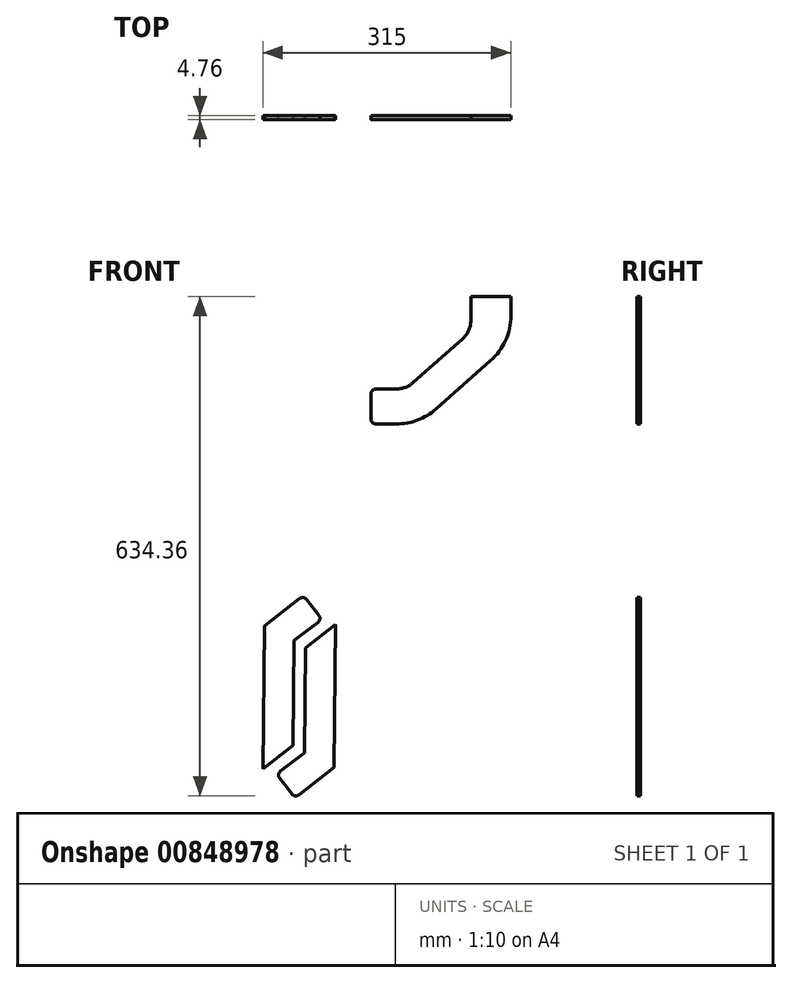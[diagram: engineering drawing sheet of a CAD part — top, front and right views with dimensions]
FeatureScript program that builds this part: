
annotation { "Feature Type Name" : "Feature", "Feature Type Description" : "" }
export const myFeature = defineFeature(function(context is Context, id is Id, definition is map)
    precondition{}
    {
        {
            var Q0;
            Q0=qCreatedBy(makeId("Front.planeOp"),FACE);
            var sketch = newSketch(context, id + "F0", { "sketchPlane" : qUnion([Q0])});
            skLineSegment(sketch, "E0.bottom", {"start": v(6.35, 0) * mm, "end": v(32.42, 0) * mm});
            skLineSegment(sketch, "E0.top", {"start": v(127, 161.93) * mm, "end": v(177.8, 161.93) * mm});
            skLineSegment(sketch, "E0.left", {"start": v(0, 6.35) * mm, "end": v(0, 38.1) * mm});
            skLineSegment(sketch, "E0.right", {"start": v(177.8, 137.4) * mm, "end": v(177.8, 161.93) * mm});
            skLineSegment(sketch, "E1", {"start": v(6.35, 44.45) * mm, "end": v(32.42, 44.45) * mm});
            skLineSegment(sketch, "E2", {"start": v(53.46, 52.42) * mm, "end": v(116.29, 108) * mm});
            skLineSegment(sketch, "E3", {"start": v(127, 131.78) * mm, "end": v(127, 161.93) * mm});
            skLineSegment(sketch, "E4.0", {"start": v(82.91, 19.13) * mm, "end": v(152.09, 80.32) * mm});
            skArc(sketch, "E5.filletArc", {"start": v(32.42, 0) * mm, "mid": v(59.42, 4.94) * mm, "end": v(82.91, 19.13) * mm});
            skArc(sketch, "E6.filletArc", {"start": v(152.09, 80.32) * mm, "mid": v(171.08, 106.1) * mm, "end": v(177.8, 137.4) * mm});
            skPoint(sketch, "E7.visualSharp", {"position": v(44.45, 44.45) * mm});
            skArc(sketch, "E7.filletArc", {"start": v(32.42, 44.45) * mm, "mid": v(43.67, 46.5) * mm, "end": v(53.46, 52.42) * mm});
            skPoint(sketch, "E8.visualSharp", {"position": v(127, 117.48) * mm});
            skArc(sketch, "E8.filletArc", {"start": v(116.29, 108) * mm, "mid": v(124.2, 118.74) * mm, "end": v(127, 131.78) * mm});
            skPoint(sketch, "E9.visualSharp", {"position": v(0, 44.45) * mm});
            skArc(sketch, "E9.filletArc", {"start": v(6.35, 44.45) * mm, "mid": v(1.86, 42.6) * mm, "end": v(0, 38.1) * mm});
            skPoint(sketch, "E10.visualSharp", {"position": v(0, 0) * mm});
            skArc(sketch, "E10.filletArc", {"start": v(0, 6.35) * mm, "mid": v(1.86, 1.86) * mm, "end": v(6.35, 0) * mm});
            skArc(sketch, "E11.MirrorCS", {"start": v(-114.78, -440.95) * mm, "mid": v(-117.2, -445.17) * mm, "end": v(-115.92, -449.86) * mm});
            skArc(sketch, "E12.MirrorCS", {"start": v(-100.4, -469.96) * mm, "mid": v(-96.18, -472.38) * mm, "end": v(-91.5, -471.11) * mm});
            skPoint(sketch, "E13.MirrorP", {"position": v(-84.62, -417.67) * mm});
            skLineSegment(sketch, "E14.MirrorCS", {"start": v(-83.27, -284.33) * mm, "end": v(-44.86, -254.68) * mm});
            skLineSegment(sketch, "E15.MirrorCS", {"start": v(-83.27, -284.33) * mm, "end": v(-84.62, -417.67) * mm});
            skLineSegment(sketch, "E16.MirrorCS", {"start": v(-114.78, -440.95) * mm, "end": v(-84.62, -417.67) * mm});
            skLineSegment(sketch, "E17.MirrorCS", {"start": v(-91.5, -471.11) * mm, "end": v(-46.7, -436.54) * mm});
            skLineSegment(sketch, "E18.MirrorCS", {"start": v(-100.4, -469.96) * mm, "end": v(-115.92, -449.86) * mm});
            skLineSegment(sketch, "E19.0", {"start": v(-44.86, -254.68) * mm, "end": v(-46.7, -436.54) * mm});
            skArc(sketch, "E20.MirrorCS", {"start": v(-81.66, -222.99) * mm, "mid": v(-85.88, -220.57) * mm, "end": v(-90.57, -221.84) * mm});
            skArc(sketch, "E21.MirrorCS", {"start": v(-67.29, -252) * mm, "mid": v(-64.87, -247.79) * mm, "end": v(-66.14, -243.1) * mm});
            skPoint(sketch, "E22.MirrorP", {"position": v(-97.45, -275.28) * mm});
            skLineSegment(sketch, "E23.MirrorCS", {"start": v(-90.57, -221.84) * mm, "end": v(-135.36, -256.42) * mm});
            skLineSegment(sketch, "E24.MirrorCS", {"start": v(-137.2, -438.27) * mm, "end": v(-135.36, -256.42) * mm});
            skLineSegment(sketch, "E25.MirrorCS", {"start": v(-98.8, -408.63) * mm, "end": v(-137.2, -438.27) * mm});
            skLineSegment(sketch, "E26.MirrorCS", {"start": v(-81.66, -222.99) * mm, "end": v(-66.14, -243.1) * mm});
            skLineSegment(sketch, "E27.MirrorCS", {"start": v(-67.29, -252) * mm, "end": v(-97.45, -275.28) * mm});
            skLineSegment(sketch, "E28.MirrorCS", {"start": v(-98.8, -408.63) * mm, "end": v(-97.45, -275.28) * mm});
            skSolve(sketch);
        }
        {
            var Q0;
            Q0 = qSketchRegion(id + "F0", true);
            extrude(context, id + "F1", {"entities" : qUnion([Q0]), "depth" : 4.76 * mm, "offsetDistance" : 25.4 * mm});
        }
    });
